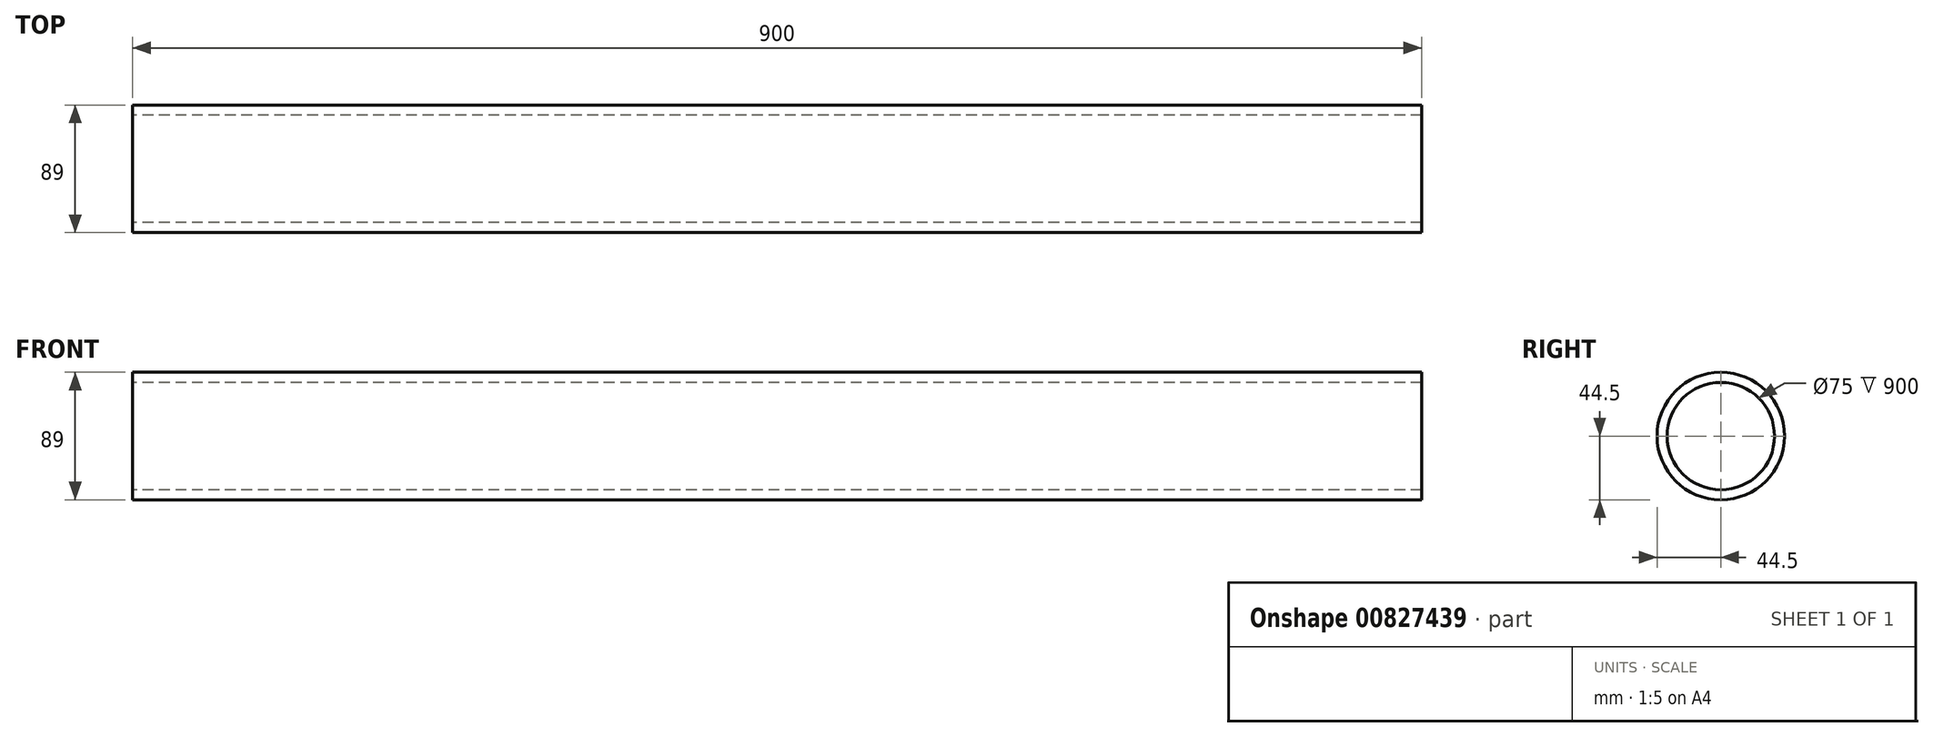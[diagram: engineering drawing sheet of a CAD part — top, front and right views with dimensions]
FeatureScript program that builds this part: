
annotation { "Feature Type Name" : "Feature", "Feature Type Description" : "" }
export const myFeature = defineFeature(function(context is Context, id is Id, definition is map)
    precondition{}
    {
        {
            var Q0;
            Q0=qCreatedBy(makeId("Right.planeOp"),FACE);
            var sketch = newSketch(context, id + "F0", { "sketchPlane" : qUnion([Q0])});
            skCircle(sketch, "E0", {"center": v(0, 0) * mm, "radius": 37.5 * mm});
            skCircle(sketch, "E1", {"center": v(0, 0) * mm, "radius": 44.5 * mm});
            skSolve(sketch);
        }
        {
            var Q0;
            Q0=makeQuery(id+"F0.imprint","IMPRINT",FACE,{"disambiguationData":[TD([[makeQuery(id+"F0.imprint","IMPRINT",EDGE,{"derivedFrom":sQuery(id+"F0.wireOp",EDGE,"E0")}),-1.0]])]});
            extrude(context, id + "F1", {"entities" : qUnion([Q0]), "depth" : 900 * mm, "offsetDistance" : 25 * mm});
        }
    });
